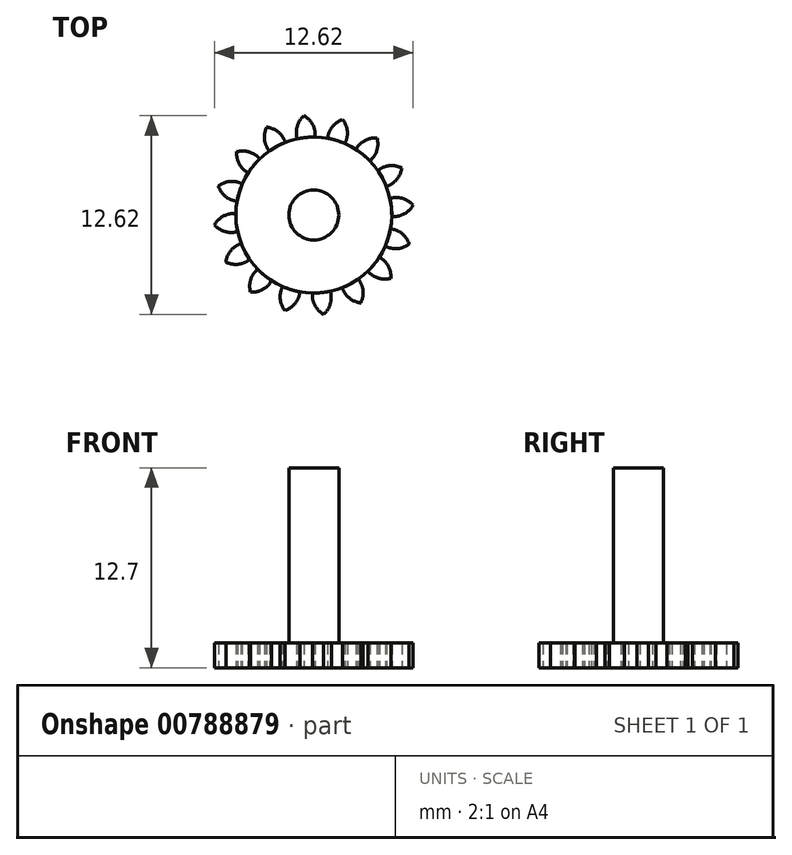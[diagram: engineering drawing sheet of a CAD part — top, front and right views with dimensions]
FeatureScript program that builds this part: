
annotation { "Feature Type Name" : "Feature", "Feature Type Description" : "" }
export const myFeature = defineFeature(function(context is Context, id is Id, definition is map)
    precondition{}
    {
        {
            var Q0;
            Q0=qCreatedBy(makeId("Top.planeOp"),FACE);
            var sketch = newSketch(context, id + "F0", { "sketchPlane" : qUnion([Q0])});
            skCircle(sketch, "E0", {"center": v(0, 0) * mm, "radius": 6.35 * mm, "construction": true});
            skCircle(sketch, "E1", {"center": v(0, 0) * mm, "radius": 5.59 * mm, "construction": true});
            skCircle(sketch, "E2", {"center": v(0, 0) * mm, "radius": 4.95 * mm});
            skLineSegment(sketch, "E3", {"start": v(0, 0) * mm, "end": v(0, 7.42) * mm, "construction": true});
            skLineSegment(sketch, "E4", {"start": v(0, 5.59) * mm, "end": v(-6.26, 5.59) * mm, "construction": true});
            skLineSegment(sketch, "E5", {"start": v(0, 0) * mm, "end": v(-0.73, 7.45) * mm, "construction": true});
            skLineSegment(sketch, "E6", {"start": v(0, 5.59) * mm, "end": v(-6.15, 3.35) * mm, "construction": true});
            skCircle(sketch, "E7", {"center": v(0, 0) * mm, "radius": 5.25 * mm, "construction": true});
            skCircle(sketch, "E8", {"center": v(0, 5.59) * mm, "radius": 1.4 * mm, "construction": true});
            skCircle(sketch, "E9", {"center": v(-1.3, 5.09) * mm, "radius": 1.4 * mm, "construction": true});
            skArc(sketch, "E10", {"start": v(0, 5.59) * mm, "mid": v(-0.26, 6) * mm, "end": v(-0.64, 6.32) * mm});
            skArc(sketch, "E11", {"start": v(0.09, 4.95) * mm, "mid": v(0.08, 5.28) * mm, "end": v(0, 5.59) * mm});
            skArc(sketch, "E12.MirrorCS", {"start": v(-1.1, 5.48) * mm, "mid": v(-0.92, 5.94) * mm, "end": v(-0.6, 6.32) * mm});
            skArc(sketch, "E13.MirrorCS", {"start": v(-1.05, 4.84) * mm, "mid": v(-1.1, 5.16) * mm, "end": v(-1.1, 5.48) * mm});
            skCircle(sketch, "E14", {"center": v(0, 0) * mm, "radius": 1.59 * mm});
            skSolve(sketch);
        }
        {
            var Q0;
            {var subQ4=sQuery(id+"F0.wireOp",EDGE,"E11");Q0=makeQuery(id+"F0.imprint","IMPRINT",FACE,{"disambiguationData":[TD([[makeQuery(id+"F0.imprint","IMPRINT",EDGE,{"derivedFrom":subQ4}),1.0]])]});}
            extrude(context, id + "F1", {"entities" : qUnion([Q0]), "depth" : 1.59 * mm, "offsetDistance" : 25.4 * mm});
        }
        {
            var Q0;
            Q0=makeQuery(id+"F1.opExtrude","SWEPT_BODY",BODY,{"disambiguationData":[OSD([sQuery(id+"F0.wireOp",EDGE,"E2"),sQuery(id+"F0.wireOp",EDGE,"E10"),sQuery(id+"F0.wireOp",EDGE,"E11"),sQuery(id+"F0.wireOp",EDGE,"E12.MirrorCS"),sQuery(id+"F0.wireOp",EDGE,"E13.MirrorCS")])]});
            var Q1;
            Q1=sQuery(id+"F0.wireOp",EDGE,"E2");
            circularPattern(context, id + "F2", {"entities" : qUnion([Q0]), "axis" : qUnion([Q1]), "angle" : 360 * degree, "instanceCount" : 16, "equalSpace" : true});
        }
        {
            var Q0;
            Q0=makeQuery(id+"F0.imprint","IMPRINT",FACE,{"disambiguationData":[TD([[makeQuery(id+"F0.imprint","IMPRINT",EDGE,{"derivedFrom":sQuery(id+"F0.wireOp",EDGE,"E14")}),-1.0]])]});
            extrude(context, id + "F3", {"entities" : qUnion([Q0]), "depth" : 1.59 * mm, "offsetDistance" : 25.4 * mm});
        }
        {
            var Q0;
            Q0=makeQuery(id+"F0.imprint","IMPRINT",FACE,{"disambiguationData":[TD([[makeQuery(id+"F0.imprint","IMPRINT",EDGE,{"derivedFrom":sQuery(id+"F0.wireOp",EDGE,"E14")}),1.0]])]});
            extrude(context, id + "F4", {"entities" : qUnion([Q0]), "operationType" : NewBodyOperationType.ADD, "depth" : 12.7 * mm, "offsetDistance" : 25.4 * mm});
        }
    });
